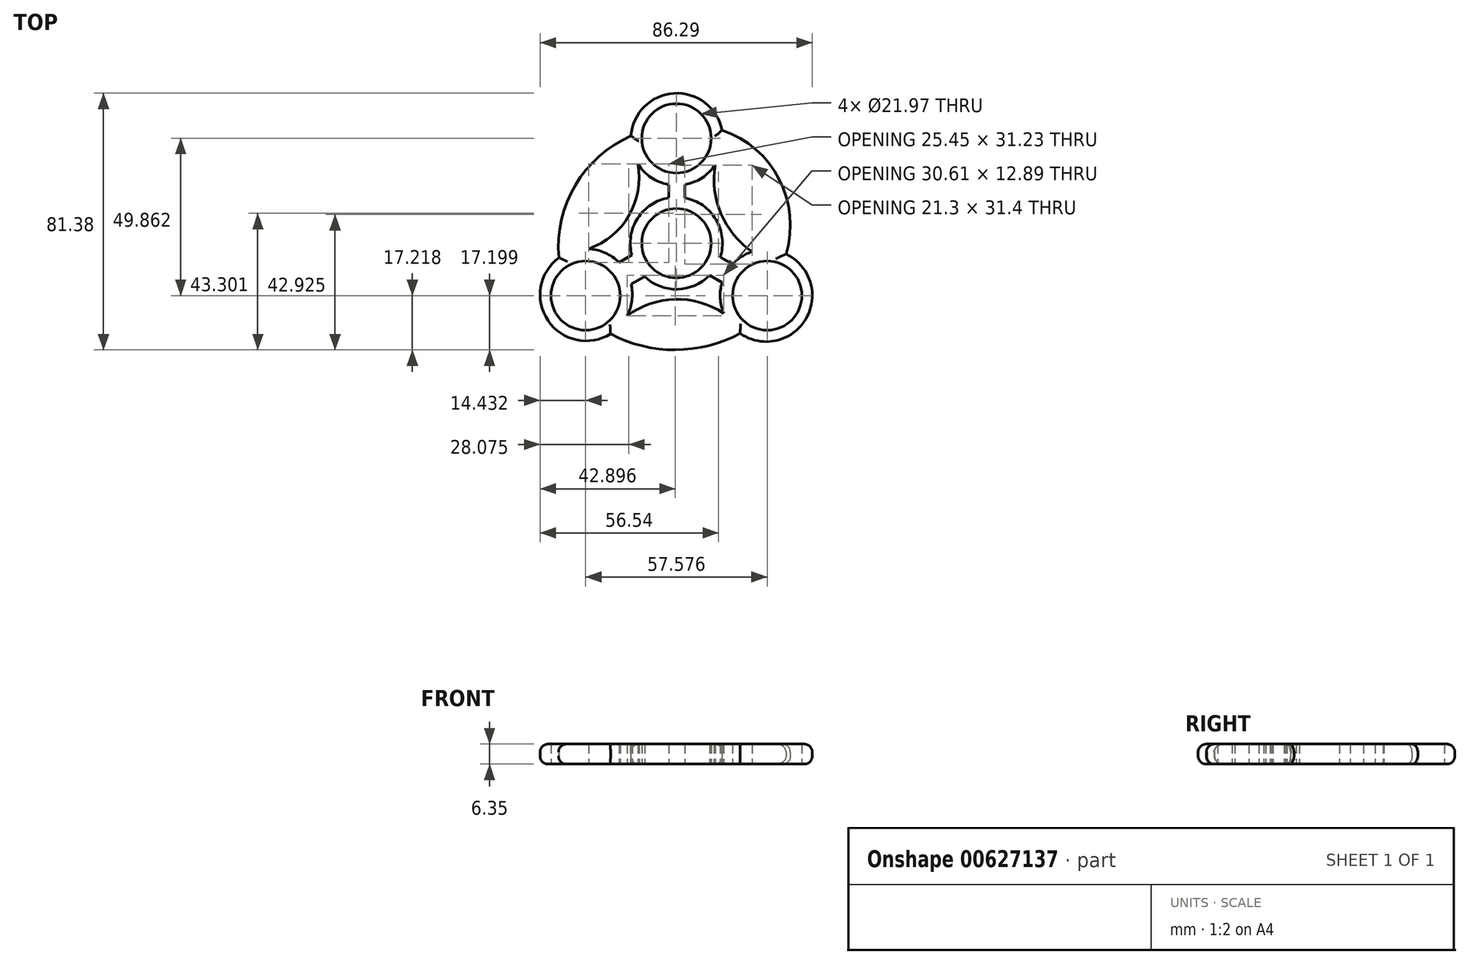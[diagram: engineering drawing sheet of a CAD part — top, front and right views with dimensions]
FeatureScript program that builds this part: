
annotation { "Feature Type Name" : "Feature", "Feature Type Description" : "" }
export const myFeature = defineFeature(function(context is Context, id is Id, definition is map)
    precondition{}
    {
        {
            var Q0;
            Q0=qCreatedBy(makeId("Top.planeOp"),FACE);
            var sketch = newSketch(context, id + "F0", { "sketchPlane" : qUnion([Q0])});
            skCircle(sketch, "E0", {"center": v(0, 0) * mm, "radius": 10.99 * mm});
            skCircle(sketch, "E1", {"center": v(0, 0) * mm, "radius": 14.6 * mm});
            skLineSegment(sketch, "E2", {"start": v(0, 0) * mm, "end": v(0, 33.24) * mm});
            skCircle(sketch, "E3", {"center": v(0, 33.24) * mm, "radius": 10.99 * mm});
            skCircle(sketch, "E4", {"center": v(0.14, 32.95) * mm, "radius": 14.6 * mm});
            skLineSegment(sketch, "E5.1.0", {"start": v(0, 0) * mm, "end": v(-28.79, -16.62) * mm});
            skCircle(sketch, "E5.1.1", {"center": v(-28.79, -16.62) * mm, "radius": 10.99 * mm});
            skCircle(sketch, "E5.1.2", {"center": v(-28.61, -16.35) * mm, "radius": 14.6 * mm});
            skLineSegment(sketch, "E5.2.0", {"start": v(0, 0) * mm, "end": v(28.79, -16.62) * mm});
            skCircle(sketch, "E5.2.1", {"center": v(28.79, -16.62) * mm, "radius": 10.99 * mm});
            skCircle(sketch, "E5.2.2", {"center": v(28.47, -16.6) * mm, "radius": 14.6 * mm});
            skArc(sketch, "E6", {"start": v(-27.87, -1.77) * mm, "mid": v(-15.06, 8.76) * mm, "end": v(-12.17, 25.1) * mm});
            skArc(sketch, "E7", {"start": v(-14.42, 34.02) * mm, "mid": v(-32.05, 18.4) * mm, "end": v(-37.25, -4.58) * mm});
            skArc(sketch, "E8", {"start": v(12.26, 24.8) * mm, "mid": v(14.13, 9.35) * mm, "end": v(23.97, -2.7) * mm});
            skArc(sketch, "E9", {"start": v(14.98, -22.21) * mm, "mid": v(-0.46, -17.79) * mm, "end": v(-15.63, -23.05) * mm});
            skArc(sketch, "E10", {"start": v(-20.88, -28.74) * mm, "mid": v(-0.34, -33.82) * mm, "end": v(20.17, -28.62) * mm});
            skLineSegment(sketch, "E11", {"start": v(-14.11, -3.75) * mm, "end": v(-18.18, -6.13) * mm});
            skLineSegment(sketch, "E12", {"start": v(-14.4, -13) * mm, "end": v(-10.03, -10.62) * mm});
            skPoint(sketch, "E12.startSnap0", {"position": v(-14.4, -8.31) * mm});
            skLineSegment(sketch, "E13", {"start": v(-2.42, 14.4) * mm, "end": v(-2.42, 18.58) * mm});
            skLineSegment(sketch, "E14", {"start": v(2.67, 14.36) * mm, "end": v(2.67, 18.57) * mm});
            skLineSegment(sketch, "E15", {"start": v(10.5, -10.16) * mm, "end": v(14.47, -12.45) * mm});
            skLineSegment(sketch, "E16", {"start": v(13.91, -4.45) * mm, "end": v(17.83, -6.6) * mm});
            skArc(sketch, "E17", {"start": v(34.77, -3.43) * mm, "mid": v(32.58, 20.31) * mm, "end": v(14.47, 35.82) * mm});
            skSolve(sketch);
        }
        {
            var Q0;
            {var subQ0=sQuery(id+"F0.wireOp",EDGE,"E6");Q0=makeQuery(id+"F0.imprint","IMPRINT",FACE,{"disambiguationData":[TD([[makeQuery(id+"F0.imprint","IMPRINT",EDGE,{"derivedFrom":subQ0}),1.0]])]});}
            var Q1;
            Q1=makeQuery(id+"F0.imprint","IMPRINT",FACE,{"disambiguationData":[TD([[makeQuery(id+"F0.imprint","IMPRINT",EDGE,{"derivedFrom":sQuery(id+"F0.wireOp",EDGE,"E5.1.1")}),-1.0]])]});
            var Q2;
            {var subQ0=sQuery(id+"F0.wireOp",EDGE,"E12");Q2=makeQuery(id+"F0.imprint","IMPRINT",FACE,{"disambiguationData":[TD([[makeQuery(id+"F0.imprint","IMPRINT",EDGE,{"derivedFrom":subQ0}),1.0]])]});}
            var Q3;
            {var subQ0=sQuery(id+"F0.wireOp",EDGE,"E11");Q3=makeQuery(id+"F0.imprint","IMPRINT",FACE,{"disambiguationData":[TD([[makeQuery(id+"F0.imprint","IMPRINT",EDGE,{"derivedFrom":subQ0}),1.0]])]});}
            var Q4;
            Q4=makeQuery(id+"F0.imprint","IMPRINT",FACE,{"disambiguationData":[TD([[makeQuery(id+"F0.imprint","IMPRINT",EDGE,{"derivedFrom":sQuery(id+"F0.wireOp",EDGE,"E3")}),-1.0]])]});
            var Q5;
            {var subQ0=sQuery(id+"F0.wireOp",EDGE,"E14");Q5=makeQuery(id+"F0.imprint","IMPRINT",FACE,{"disambiguationData":[TD([[makeQuery(id+"F0.imprint","IMPRINT",EDGE,{"derivedFrom":subQ0}),1.0]])]});}
            var Q6;
            {var subQ0=sQuery(id+"F0.wireOp",EDGE,"E13");Q6=makeQuery(id+"F0.imprint","IMPRINT",FACE,{"disambiguationData":[TD([[makeQuery(id+"F0.imprint","IMPRINT",EDGE,{"derivedFrom":subQ0}),-1.0]])]});}
            var Q7;
            {var subQ2=sQuery(id+"F0.wireOp",EDGE,"E5.1.0");var subQ7=sQuery(id+"F0.wireOp",EDGE,"E0");var subQ8=makeQuery(id+"F0.imprint","INTERSECT",VERTEX,{"derivedFrom":[subQ7,subQ2]});Q7=makeQuery(id+"F0.imprint","IMPRINT",FACE,{"disambiguationData":[TD([[makeQuery(id+"F0.imprint","IMPRINT",EDGE,{"disambiguationData":[TD([[subQ8,1.0]])],"derivedFrom":subQ7}),-1.0]])]});}
            var Q8;
            {var subQ5=sQuery(id+"F0.wireOp",EDGE,"E2");var subQ7=sQuery(id+"F0.wireOp",EDGE,"E0");var subQ8=makeQuery(id+"F0.imprint","INTERSECT",VERTEX,{"derivedFrom":[subQ7,subQ5]});Q8=makeQuery(id+"F0.imprint","IMPRINT",FACE,{"disambiguationData":[TD([[makeQuery(id+"F0.imprint","IMPRINT",EDGE,{"disambiguationData":[TD([[subQ8,1.0]])],"derivedFrom":subQ7}),-1.0]])]});}
            var Q9;
            {var subQ5=sQuery(id+"F0.wireOp",EDGE,"E5.1.0");var subQ7=sQuery(id+"F0.wireOp",EDGE,"E0");var subQ8=makeQuery(id+"F0.imprint","INTERSECT",VERTEX,{"derivedFrom":[subQ7,subQ5]});Q9=makeQuery(id+"F0.imprint","IMPRINT",FACE,{"disambiguationData":[TD([[makeQuery(id+"F0.imprint","IMPRINT",EDGE,{"disambiguationData":[TD([[subQ8,-1.0]])],"derivedFrom":subQ7}),-1.0]])]});}
            var Q10;
            {var subQ0=sQuery(id+"F0.wireOp",EDGE,"E9");Q10=makeQuery(id+"F0.imprint","IMPRINT",FACE,{"disambiguationData":[TD([[makeQuery(id+"F0.imprint","IMPRINT",EDGE,{"derivedFrom":subQ0}),1.0]])]});}
            var Q11;
            {var subQ0=sQuery(id+"F0.wireOp",EDGE,"E15");Q11=makeQuery(id+"F0.imprint","IMPRINT",FACE,{"disambiguationData":[TD([[makeQuery(id+"F0.imprint","IMPRINT",EDGE,{"derivedFrom":subQ0}),1.0]])]});}
            var Q12;
            {var subQ0=sQuery(id+"F0.wireOp",EDGE,"E16");Q12=makeQuery(id+"F0.imprint","IMPRINT",FACE,{"disambiguationData":[TD([[makeQuery(id+"F0.imprint","IMPRINT",EDGE,{"derivedFrom":subQ0}),-1.0]])]});}
            var Q13;
            Q13=makeQuery(id+"F0.imprint","IMPRINT",FACE,{"disambiguationData":[TD([[makeQuery(id+"F0.imprint","IMPRINT",EDGE,{"derivedFrom":sQuery(id+"F0.wireOp",EDGE,"E5.2.1")}),-1.0]])]});
            var Q14;
            {var subQ0=sQuery(id+"F0.wireOp",EDGE,"E8");Q14=makeQuery(id+"F0.imprint","IMPRINT",FACE,{"disambiguationData":[TD([[makeQuery(id+"F0.imprint","IMPRINT",EDGE,{"derivedFrom":subQ0}),1.0]])]});}
            extrude(context, id + "F1", {"entities" : qUnion([Q0, Q1, Q2, Q3, Q4, Q5, Q6, Q7, Q8, Q9, Q10, Q11, Q12, Q13, Q14]), "depth" : 6.35 * mm, "offsetDistance" : 25.4 * mm});
        }
        {
            var Q0;
            Q0=makeQuery(id+"F1.opExtrude","CAP_EDGE",EDGE,{"disambiguationData":[OSD([sQuery(id+"F0.wireOp",EDGE,"E7")])],"isStart":false});
            var Q1;
            {var subQ0=sQuery(id+"F0.wireOp",EDGE,"E5.1.2");Q1=makeQuery(id+"F1.opExtrude","CAP_EDGE",EDGE,{"disambiguationData":[OSD([subQ0]),TDD([makeQuery(id+"F0.imprint","IMPRINT",EDGE,{"disambiguationData":[TD([[makeQuery(id+"F0.imprint","INTERSECT",VERTEX,{"derivedFrom":[subQ0,sQuery(id+"F0.wireOp",EDGE,"E7")]}),-1.0]])],"derivedFrom":subQ0})])],"isStart":false});}
            var Q2;
            Q2=makeQuery(id+"F1.opExtrude","CAP_EDGE",EDGE,{"disambiguationData":[OSD([sQuery(id+"F0.wireOp",EDGE,"E10")])],"isStart":false});
            var Q3;
            {var subQ0=sQuery(id+"F0.wireOp",EDGE,"E5.2.2");Q3=makeQuery(id+"F1.opExtrude","CAP_EDGE",EDGE,{"disambiguationData":[OSD([subQ0]),TDD([makeQuery(id+"F0.imprint","IMPRINT",EDGE,{"disambiguationData":[TD([[makeQuery(id+"F0.imprint","INTERSECT",VERTEX,{"derivedFrom":[subQ0,sQuery(id+"F0.wireOp",EDGE,"E10")]}),-1.0]])],"derivedFrom":subQ0})])],"isStart":false});}
            var Q4;
            Q4=makeQuery(id+"F1.opExtrude","CAP_EDGE",EDGE,{"disambiguationData":[OSD([sQuery(id+"F0.wireOp",EDGE,"E17")])],"isStart":false});
            var Q5;
            {var subQ0=sQuery(id+"F0.wireOp",EDGE,"E4");Q5=makeQuery(id+"F1.opExtrude","CAP_EDGE",EDGE,{"disambiguationData":[OSD([subQ0]),TDD([makeQuery(id+"F0.imprint","IMPRINT",EDGE,{"disambiguationData":[TD([[makeQuery(id+"F0.imprint","INTERSECT",VERTEX,{"derivedFrom":[subQ0,sQuery(id+"F0.wireOp",EDGE,"E7")]}),1.0]])],"derivedFrom":subQ0})])],"isStart":false});}
            var Q6;
            {var subQ0=sQuery(id+"F0.wireOp",EDGE,"E5.2.2");Q6=makeQuery(id+"F1.opExtrude","CAP_EDGE",EDGE,{"disambiguationData":[OSD([subQ0]),TDD([makeQuery(id+"F0.imprint","IMPRINT",EDGE,{"disambiguationData":[TD([[makeQuery(id+"F0.imprint","INTERSECT",VERTEX,{"derivedFrom":[subQ0,sQuery(id+"F0.wireOp",EDGE,"E10")]}),-1.0]])],"derivedFrom":subQ0})])],"isStart":true});}
            var Q7;
            Q7=makeQuery(id+"F1.opExtrude","CAP_EDGE",EDGE,{"disambiguationData":[OSD([sQuery(id+"F0.wireOp",EDGE,"E10")])],"isStart":true});
            var Q8;
            Q8=makeQuery(id+"F1.opExtrude","CAP_EDGE",EDGE,{"disambiguationData":[OSD([sQuery(id+"F0.wireOp",EDGE,"E7")])],"isStart":true});
            var Q9;
            {var subQ0=sQuery(id+"F0.wireOp",EDGE,"E4");Q9=makeQuery(id+"F1.opExtrude","CAP_EDGE",EDGE,{"disambiguationData":[OSD([subQ0]),TDD([makeQuery(id+"F0.imprint","IMPRINT",EDGE,{"disambiguationData":[TD([[makeQuery(id+"F0.imprint","INTERSECT",VERTEX,{"derivedFrom":[subQ0,sQuery(id+"F0.wireOp",EDGE,"E7")]}),1.0]])],"derivedFrom":subQ0})])],"isStart":true});}
            var Q10;
            Q10=makeQuery(id+"F1.opExtrude","CAP_EDGE",EDGE,{"disambiguationData":[OSD([sQuery(id+"F0.wireOp",EDGE,"E17")])],"isStart":true});
            var Q11;
            {var subQ0=sQuery(id+"F0.wireOp",EDGE,"E5.1.2");Q11=makeQuery(id+"F1.opExtrude","CAP_EDGE",EDGE,{"disambiguationData":[OSD([subQ0]),TDD([makeQuery(id+"F0.imprint","IMPRINT",EDGE,{"disambiguationData":[TD([[makeQuery(id+"F0.imprint","INTERSECT",VERTEX,{"derivedFrom":[subQ0,sQuery(id+"F0.wireOp",EDGE,"E7")]}),-1.0]])],"derivedFrom":subQ0})])],"isStart":true});}
            fillet(context, id + "F2", {"entities" : qUnion([Q0, Q1, Q2, Q3, Q4, Q5, Q6, Q7, Q8, Q9, Q10, Q11]), "radius" : 2.54 * mm, "tangentPropagation" : true, "allowEdgeOverflow" : false});
        }
    });
